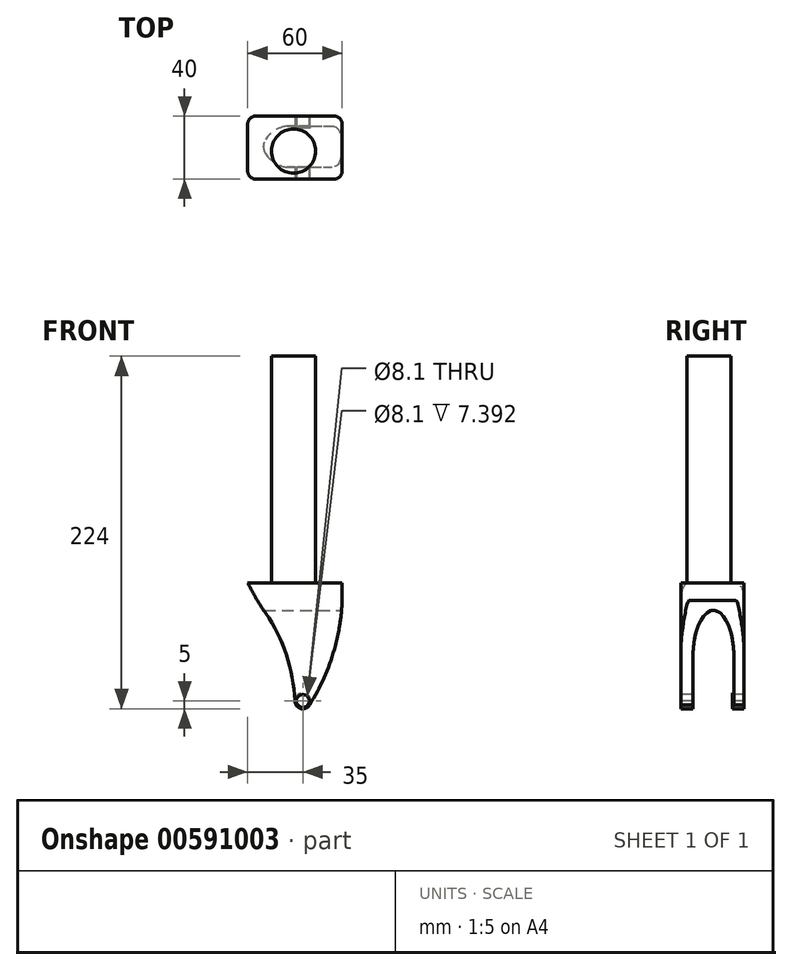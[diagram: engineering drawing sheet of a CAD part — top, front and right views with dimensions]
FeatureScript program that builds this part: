
annotation { "Feature Type Name" : "Feature", "Feature Type Description" : "" }
export const myFeature = defineFeature(function(context is Context, id is Id, definition is map)
    precondition{}
    {
        {
            var Q0;
            Q0=qCreatedBy(makeId("Top.planeOp"),FACE);
            var sketch = newSketch(context, id + "F0", { "sketchPlane" : qUnion([Q0])});
            skCircle(sketch, "E0", {"center": v(0, 0) * mm, "radius": 14 * mm});
            skSolve(sketch);
        }
        {
            var Q0;
            Q0 = qSketchRegion(id + "F0", true);
            extrude(context, id + "F1", {"entities" : qUnion([Q0]), "depth" : 144 * mm, "offsetDistance" : 25 * mm});
        }
        {
            var Q0;
            Q0=qCreatedBy(makeId("Top.planeOp"),FACE);
            var sketch = newSketch(context, id + "F2", { "sketchPlane" : qUnion([Q0])});
            skLineSegment(sketch, "E1.bottom", {"start": v(-29.15, 22.22) * mm, "end": v(30.85, 22.22) * mm});
            skLineSegment(sketch, "E1.top", {"start": v(-29.15, -17.78) * mm, "end": v(30.85, -17.78) * mm});
            skLineSegment(sketch, "E1.left", {"start": v(-29.15, 22.22) * mm, "end": v(-29.15, -17.78) * mm});
            skLineSegment(sketch, "E1.right", {"start": v(30.85, 22.22) * mm, "end": v(30.85, -17.78) * mm});
            skSolve(sketch);
        }
        {
            var Q0;
            Q0 = qSketchRegion(id + "F2", true);
            extrude(context, id + "F3", {"entities" : qUnion([Q0]), "operationType" : NewBodyOperationType.ADD, "oppositeDirection" : true, "depth" : 80 * mm, "offsetDistance" : 25 * mm});
        }
        {
            var Q0;
            Q0=makeQuery(id+"F3.opExtrude","SWEPT_EDGE",EDGE,{"disambiguationData":[OSD([sQuery(id+"F2.wireOp",EDGE,"E1.top"),sQuery(id+"F2.wireOp",EDGE,"E1.left")])]});
            var Q1;
            Q1=makeQuery(id+"F3.opExtrude","SWEPT_EDGE",EDGE,{"disambiguationData":[OSD([sQuery(id+"F2.wireOp",EDGE,"E1.bottom"),sQuery(id+"F2.wireOp",EDGE,"E1.left")])]});
            var Q2;
            Q2=makeQuery(id+"F3.opExtrude","SWEPT_EDGE",EDGE,{"disambiguationData":[OSD([sQuery(id+"F2.wireOp",EDGE,"E1.bottom"),sQuery(id+"F2.wireOp",EDGE,"E1.right")])]});
            var Q3;
            Q3=makeQuery(id+"F3.opExtrude","SWEPT_EDGE",EDGE,{"disambiguationData":[OSD([sQuery(id+"F2.wireOp",EDGE,"E1.top"),sQuery(id+"F2.wireOp",EDGE,"E1.right")])]});
            fillet(context, id + "F4", {"entities" : qUnion([Q0, Q1, Q2, Q3]), "radius" : 5 * mm, "tangentPropagation" : true, "allowEdgeOverflow" : false});
        }
        {
            var Q0;
            Q0=qCreatedBy(makeId("Front.planeOp"),FACE);
            var sketch = newSketch(context, id + "F5", { "sketchPlane" : qUnion([Q0])});
            skLineSegment(sketch, "E2", {"start": v(-29.15, 0) * mm, "end": v(-29.15, -90) * mm});
            skLineSegment(sketch, "E3", {"start": v(-29.15, -90) * mm, "end": v(30.85, -90) * mm});
            skLineSegment(sketch, "E4", {"start": v(30.85, -90) * mm, "end": v(30.85, 0) * mm});
            skArc(sketch, "E5", {"start": v(-29.15, 0) * mm, "mid": v(-23.74, -9.8) * mm, "end": v(-17.74, -19.25) * mm});
            skArc(sketch, "E6", {"start": v(0.85, -74.91) * mm, "mid": v(-4.59, -45.8) * mm, "end": v(-17.74, -19.25) * mm});
            skArc(sketch, "E7", {"start": v(10.2, -77.45) * mm, "mid": v(26.4, -40.3) * mm, "end": v(30.85, 0) * mm});
            skArc(sketch, "E8", {"start": v(0.85, -74.91) * mm, "mid": v(4.54, -79.83) * mm, "end": v(10.2, -77.45) * mm});
            skSolve(sketch);
        }
        {
            var Q0;
            Q0 = qSketchRegion(id + "F5", true);
            extrude(context, id + "F6", {"entities" : qUnion([Q0]), "operationType" : NewBodyOperationType.REMOVE, "endBound" : BoundingType.SYMMETRIC, "oppositeDirection" : true, "depth" : 80 * mm, "offsetDistance" : 25 * mm});
        }
        {
            var Q0;
            Q0=qCreatedBy(makeId("Right.planeOp"),FACE);
            var sketch = newSketch(context, id + "F7", { "sketchPlane" : qUnion([Q0])});
            skEllipticalArc(sketch, "E9", {});
            skLineSegment(sketch, "E10", {"start": v(-10.17, -47.45) * mm, "end": v(-10.17, -80) * mm});
            skLineSegment(sketch, "E11", {"start": v(15.82, -47.45) * mm, "end": v(15.82, -80.31) * mm});
            skLineSegment(sketch, "E12", {"start": v(15.82, -80.31) * mm, "end": v(-10.17, -80) * mm});
            const initialGuessF7  = {"E9": [0.0028250738978385925, -0.047449342839417256, 0, -1, 0.03, 0.012999064776361645, 1.5707963267948968, 4.71238898038469]};
            skSetInitialGuess(sketch, initialGuessF7);
            skSolve(sketch);
        }
        {
            var Q0;
            Q0 = qSketchRegion(id + "F7", true);
            extrude(context, id + "F8", {"entities" : qUnion([Q0]), "operationType" : NewBodyOperationType.REMOVE, "endBound" : BoundingType.SYMMETRIC, "oppositeDirection" : true, "depth" : 70 * mm, "offsetDistance" : 25 * mm});
        }
        {
            var Q0;
            Q0=makeQuery(id+"F3.opExtrude","SWEPT_FACE",FACE,{"disambiguationData":[OSD([sQuery(id+"F2.wireOp",EDGE,"E1.top")])]});
            var sketch = newSketch(context, id + "F9", { "sketchPlane" : qUnion([Q0])});
            skPoint(sketch, "E13", {"position": v(5.85, -75) * mm});
            skSolve(sketch);
        }
        {
            var Q0;
            Q0=sQuery(id+"F9.wireOp",VERTEX,"E13");
            var Q1;
            Q1=makeQuery(id+"F1.opExtrude","SWEPT_BODY",BODY,{"disambiguationData":[OSD([sQuery(id+"F0.wireOp",EDGE,"E0")])]});
            hole(context, id + "F10", {"style" : HoleStyle.SIMPLE, "endStyle" : HoleEndStyle.THROUGH, "holeDiameter" : 8.1 * mm, "majorDiameter" : 5 * mm, "isTappedThrough" : true, "tappedDepth" : 12 * mm, "tapClearance" : 3, "locations" : qUnion([Q0]), "scope" : qUnion([Q1])});
        }
        {
            var Q0;
            Q0=makeQuery(id+"F8.boolean.opBoolean","COPY",FACE,{"derivedFrom":makeQuery(id+"F8.opExtrude","SWEPT_FACE",FACE,{"disambiguationData":[OSD([sQuery(id+"F7.wireOp",EDGE,"E11")])]})});
            var sketch = newSketch(context, id + "F11", { "sketchPlane" : qUnion([Q0])});
            skCircle(sketch, "E14.0", {"center": v(5.85, -75) * mm, "radius": 5.05 * mm});
            skSolve(sketch);
        }
        {
            var Q0;
            {var subQ0=makeQuery(id+"F8.opExtrude","SWEPT_FACE",FACE,{"disambiguationData":[OSD([sQuery(id+"F7.wireOp",EDGE,"E11")])]});var subQ1=sQuery(id+"F5.wireOp",EDGE,"E8");var subQ2=makeQuery(id+"F8.boolean.opBoolean","INTERSECT",EDGE,{"derivedFrom":[makeQuery(id+"F6.boolean.opBoolean","COPY",FACE,{"derivedFrom":makeQuery(id+"F6.opExtrude","SWEPT_FACE",FACE,{"disambiguationData":[OSD([subQ1])]})}),subQ0]});Q0=makeQuery(id+"F11.imprint","IMPRINT",FACE,{"disambiguationData":[TD([[makeQuery(id+"F11.imprint","IMPRINT",EDGE,{"derivedFrom":subQ2}),-1.0]])]});}
            var Q1;
            Q1=sQuery(id+"F11.wireOp",EDGE,"E14.0");
            extrude(context, id + "F12", {"entities" : qUnion([Q0]), "operationType" : NewBodyOperationType.ADD, "surfaceOperationType" : NewSurfaceOperationType.ADD, "surfaceEntities" : qUnion([Q1]), "depth" : 1 * mm, "offsetDistance" : 25 * mm});
        }
    });
